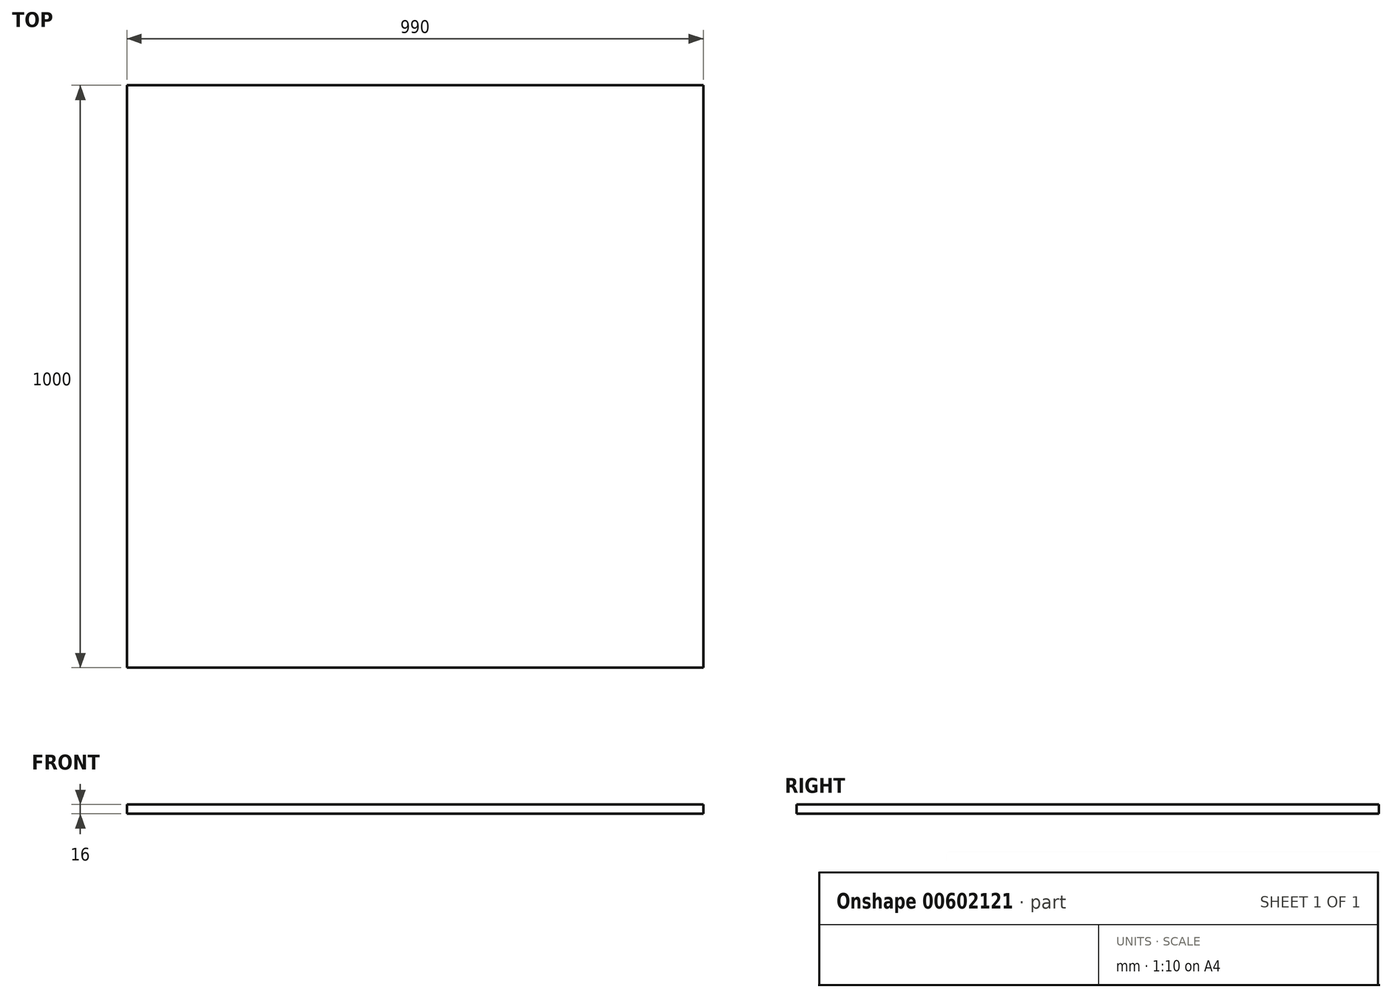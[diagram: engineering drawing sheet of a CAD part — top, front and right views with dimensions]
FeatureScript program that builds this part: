
annotation { "Feature Type Name" : "Feature", "Feature Type Description" : "" }
export const myFeature = defineFeature(function(context is Context, id is Id, definition is map)
    precondition{}
    {
        {
            var Q0;
            Q0=qCreatedBy(makeId("Top.planeOp"),FACE);
            var sketch = newSketch(context, id + "F0", { "sketchPlane" : qUnion([Q0])});
            skLineSegment(sketch, "E0.bottom", {"start": v(0, 0) * mm, "end": v(990, 0) * mm});
            skLineSegment(sketch, "E0.top", {"start": v(0, -1000) * mm, "end": v(990, -1000) * mm});
            skLineSegment(sketch, "E0.left", {"start": v(0, 0) * mm, "end": v(0, -1000) * mm});
            skLineSegment(sketch, "E0.right", {"start": v(990, 0) * mm, "end": v(990, -1000) * mm});
            skSolve(sketch);
        }
        {
            var Q0;
            Q0=qSketchRegion(id+"F0",true);
            extrude(context, id + "F1", {"entities" : qUnion([Q0]), "depth" : 16 * mm, "offsetDistance" : 25 * mm});
        }
    });
